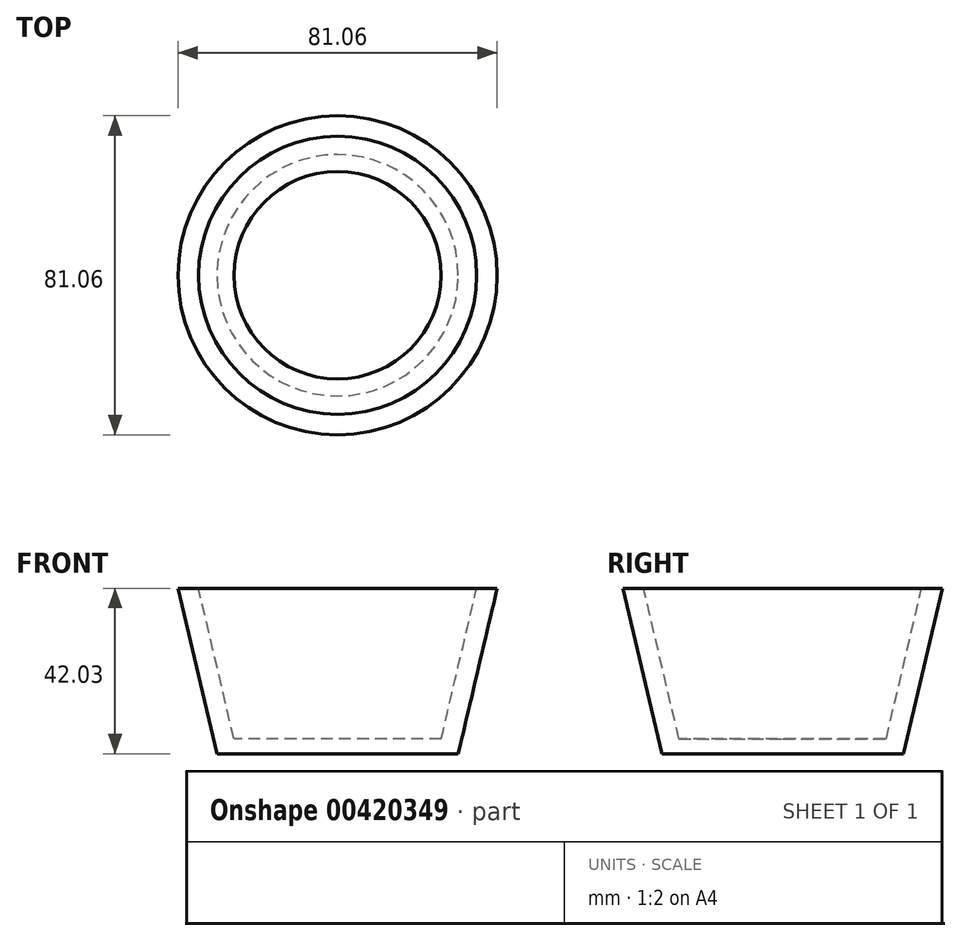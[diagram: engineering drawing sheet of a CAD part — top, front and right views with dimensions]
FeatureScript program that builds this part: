
annotation { "Feature Type Name" : "Feature", "Feature Type Description" : "" }
export const myFeature = defineFeature(function(context is Context, id is Id, definition is map)
    precondition{}
    {
        {
            var Q0;
            Q0=qCreatedBy(makeId("Front.planeOp"),FACE);
            var sketch = newSketch(context, id + "F0", { "sketchPlane" : qUnion([Q0])});
            skLineSegment(sketch, "E0", {"start": v(0, 0) * mm, "end": v(30.65, 0) * mm});
            skLineSegment(sketch, "E1", {"start": v(30.65, 0) * mm, "end": v(40.53, 42.03) * mm});
            skLineSegment(sketch, "E2", {"start": v(40.53, 42.03) * mm, "end": v(35.31, 42.03) * mm});
            skLineSegment(sketch, "E3", {"start": v(35.31, 42.03) * mm, "end": v(26.33, 3.8) * mm});
            skLineSegment(sketch, "E4", {"start": v(26.33, 3.81) * mm, "end": v(0, 3.8) * mm});
            skLineSegment(sketch, "E5", {"start": v(0, 3.8) * mm, "end": v(0, 0) * mm});
            skSolve(sketch);
        }
        {
            var Q0;
            Q0=makeQuery(id+"F0.imprint","IMPRINT",FACE,{"disambiguationData":[TD([[makeQuery(id+"F0.imprint","IMPRINT",EDGE,{"derivedFrom":sQuery(id+"F0.wireOp",EDGE,"E0")}),1.0]])]});
            var Q1;
            Q1=sQuery(id+"F0.wireOp",EDGE,"E5");
            revolve(context, id + "F1", {"entities" : qUnion([Q0]), "axis" : qUnion([Q1]), "revolveType" : RevolveType.FULL});
        }
    });
